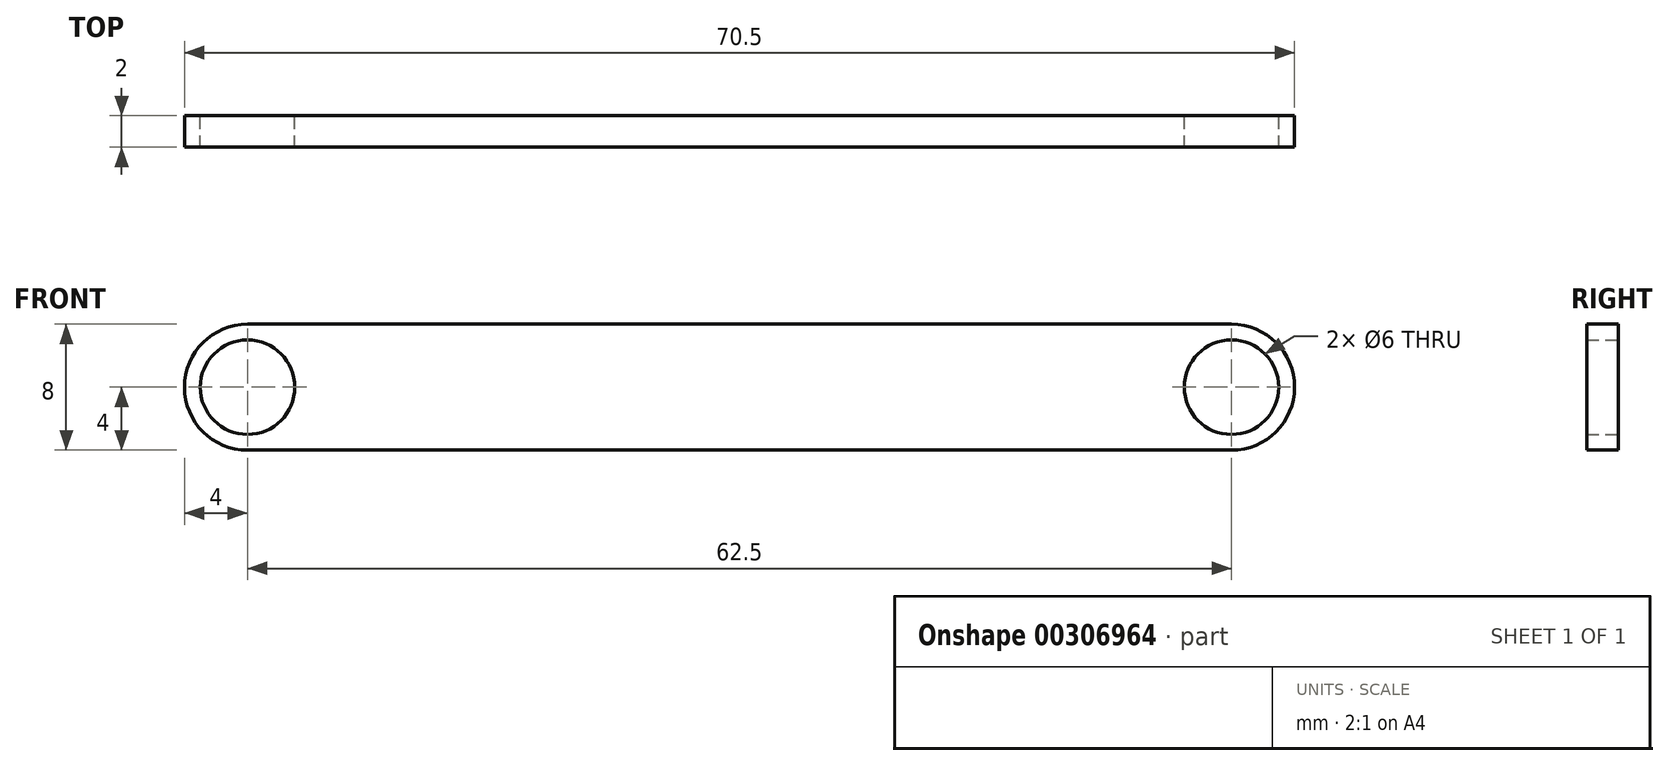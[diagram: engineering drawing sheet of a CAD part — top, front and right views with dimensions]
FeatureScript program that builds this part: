
annotation { "Feature Type Name" : "Feature", "Feature Type Description" : "" }
export const myFeature = defineFeature(function(context is Context, id is Id, definition is map)
    precondition{}
    {
        {
            var Q0;
            Q0=qCreatedBy(makeId("Front.planeOp"),FACE);
            var sketch = newSketch(context, id + "F0", { "sketchPlane" : qUnion([Q0])});
            skCircle(sketch, "E0", {"center": v(-31.25, 0) * mm, "radius": 3 * mm});
            skCircle(sketch, "E1", {"center": v(31.25, 0) * mm, "radius": 3 * mm});
            skArc(sketch, "E2", {"start": v(-31.25, 4) * mm, "mid": v(-35.25, 0) * mm, "end": v(-31.25, -4) * mm});
            skArc(sketch, "E3", {"start": v(31.25, -4) * mm, "mid": v(35.25, 0) * mm, "end": v(31.25, 4) * mm});
            skLineSegment(sketch, "E4", {"start": v(-31.25, 4) * mm, "end": v(31.25, 4) * mm});
            skLineSegment(sketch, "E5", {"start": v(-31.25, -4) * mm, "end": v(31.25, -4) * mm});
            skSolve(sketch);
        }
        {
            var Q0;
            Q0=qSketchRegion(id+"F0",true);
            extrude(context, id + "F1", {"entities" : qUnion([Q0]), "depth" : 2 * mm});
        }
    });
